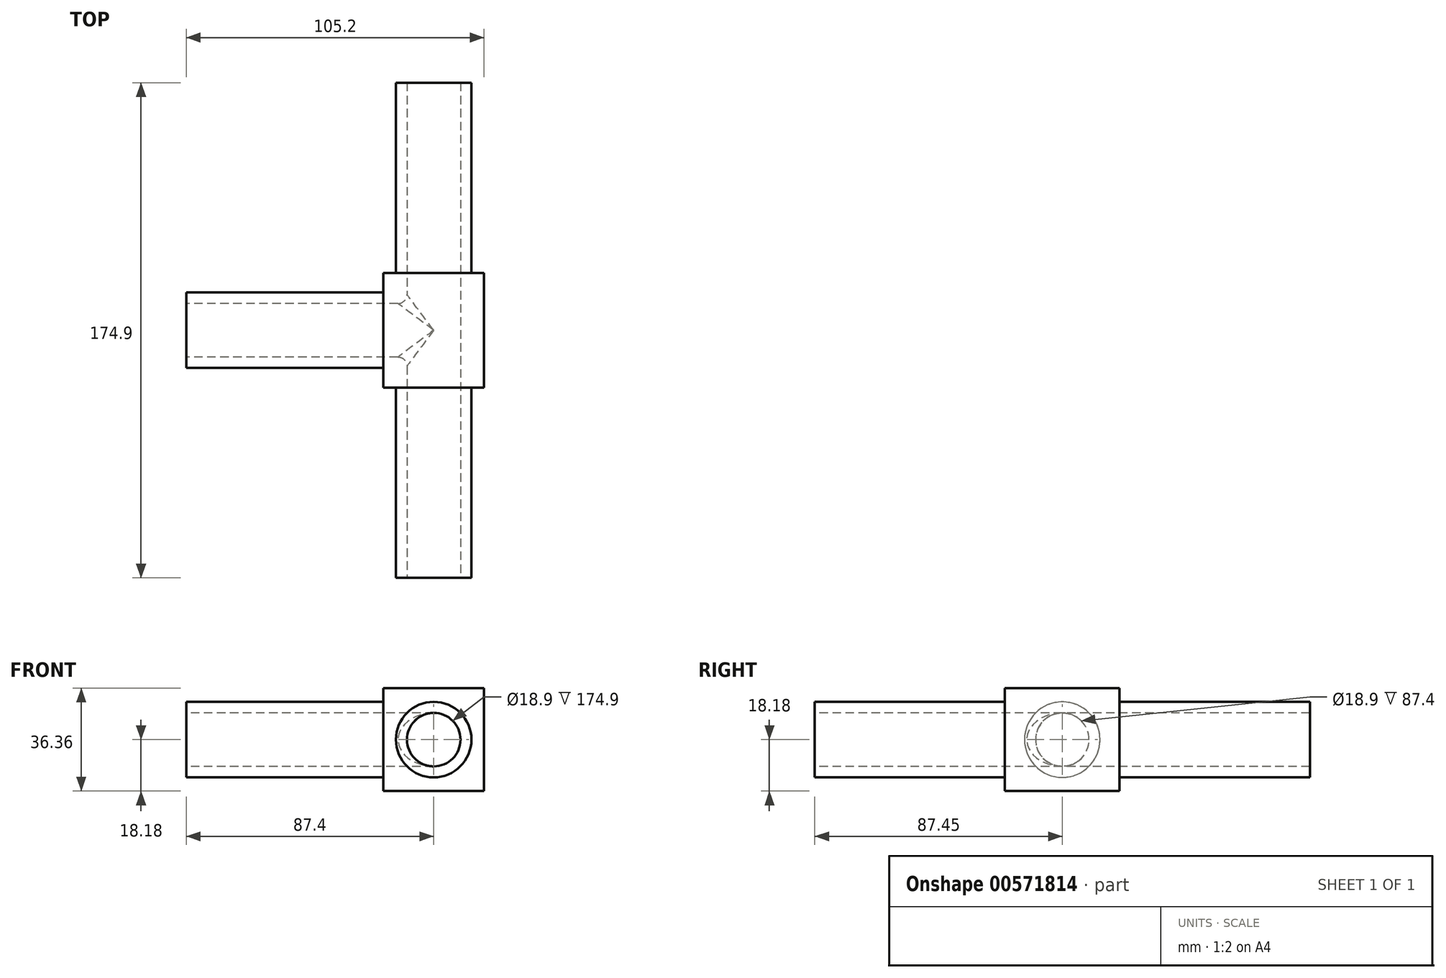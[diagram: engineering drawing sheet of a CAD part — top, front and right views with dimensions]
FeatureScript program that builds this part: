
annotation { "Feature Type Name" : "Feature", "Feature Type Description" : "" }
export const myFeature = defineFeature(function(context is Context, id is Id, definition is map)
    precondition{}
    {
        {
            var Q0;
            Q0=qCreatedBy(makeId("Front.planeOp"),FACE);
            var sketch = newSketch(context, id + "F0", { "sketchPlane" : qUnion([Q0])});
            skLineSegment(sketch, "E0.bottom", {"start": v(-17.8, -18.18) * mm, "end": v(17.8, -18.18) * mm});
            skLineSegment(sketch, "E0.top", {"start": v(-17.8, 18.18) * mm, "end": v(17.8, 18.18) * mm});
            skLineSegment(sketch, "E0.left", {"start": v(-17.8, -18.18) * mm, "end": v(-17.8, 18.18) * mm});
            skLineSegment(sketch, "E0.right", {"start": v(17.8, -18.18) * mm, "end": v(17.8, 18.18) * mm});
            skPoint(sketch, "E0.middle", {"position": v(0, 0) * mm});
            skSolve(sketch);
        }
        {
            var Q0;
            Q0 = qSketchRegion(id + "F0", true);
            extrude(context, id + "F1", {"entities" : qUnion([Q0]), "endBound" : BoundingType.SYMMETRIC, "depth" : 174.9 * mm, "offsetDistance" : 25 * mm});
        }
        {
            var Q0;
            Q0=makeQuery(id+"F1.opExtrude","CAP_FACE",FACE,{"disambiguationData":[OSD([sQuery(id+"F0.wireOp",EDGE,"E0.bottom"),sQuery(id+"F0.wireOp",EDGE,"E0.top"),sQuery(id+"F0.wireOp",EDGE,"E0.left"),sQuery(id+"F0.wireOp",EDGE,"E0.right")])],"isStart":false});
            var sketch = newSketch(context, id + "F2", { "sketchPlane" : qUnion([Q0])});
            skCircle(sketch, "E1", {"center": v(0, 0) * mm, "radius": 9.45 * mm});
            skSolve(sketch);
        }
        {
            var Q0;
            Q0 = qSketchRegion(id + "F2", true);
            extrude(context, id + "F3", {"entities" : qUnion([Q0]), "operationType" : NewBodyOperationType.REMOVE, "oppositeDirection" : true, "depth" : 206.4 * mm, "offsetDistance" : 25 * mm});
        }
        {
            var Q0;
            Q0=qCreatedBy(makeId("Right.planeOp"),FACE);
            var sketch = newSketch(context, id + "F4", { "sketchPlane" : qUnion([Q0])});
            skCircle(sketch, "E2", {"center": v(0, 0) * mm, "radius": 13.34 * mm});
            skSolve(sketch);
        }
        {
            var Q0;
            Q0 = qSketchRegion(id + "F4", true);
            extrude(context, id + "F5", {"entities" : qUnion([Q0]), "operationType" : NewBodyOperationType.ADD, "oppositeDirection" : true, "depth" : 87.4 * mm, "offsetDistance" : 25 * mm});
        }
        {
            var Q0;
            Q0=makeQuery(id+"F5.opExtrude","CAP_FACE",FACE,{"disambiguationData":[OSD([sQuery(id+"F4.wireOp",EDGE,"E2")])],"isStart":false});
            var sketch = newSketch(context, id + "F6", { "sketchPlane" : qUnion([Q0])});
            skCircle(sketch, "E3", {"center": v(0, 0) * mm, "radius": 9.45 * mm});
            skSolve(sketch);
        }
        {
            var Q0;
            Q0 = qSketchRegion(id + "F6", true);
            extrude(context, id + "F7", {"entities" : qUnion([Q0]), "operationType" : NewBodyOperationType.REMOVE, "oppositeDirection" : true, "depth" : 87.4 * mm, "offsetDistance" : 25 * mm});
        }
        {
            var Q0;
            Q0=makeQuery(id+"F1.opExtrude","CAP_FACE",FACE,{"disambiguationData":[OSD([sQuery(id+"F0.wireOp",EDGE,"E0.bottom"),sQuery(id+"F0.wireOp",EDGE,"E0.top"),sQuery(id+"F0.wireOp",EDGE,"E0.left"),sQuery(id+"F0.wireOp",EDGE,"E0.right")])],"isStart":false});
            var sketch = newSketch(context, id + "F8", { "sketchPlane" : qUnion([Q0])});
            skCircle(sketch, "E4", {"center": v(0, 0) * mm, "radius": 9.45 * mm});
            skSolve(sketch);
        }
        {
            var Q0;
            Q0 = qSketchRegion(id + "F8", true);
            extrude(context, id + "F9", {"entities" : qUnion([Q0]), "operationType" : NewBodyOperationType.REMOVE, "oppositeDirection" : true, "depth" : 231.3 * mm, "offsetDistance" : 25 * mm});
        }
        {
            var Q0;
            Q0=makeQuery(id+"F9.boolean.opBoolean","INTERSECT",EDGE,{"disambiguationData":[OD(1.0)],"derivedFrom":[makeQuery(id+"F7.boolean.opBoolean","COPY",FACE,{"derivedFrom":makeQuery(id+"F7.opExtrude","SWEPT_FACE",FACE,{"disambiguationData":[OSD([sQuery(id+"F6.wireOp",EDGE,"E3")])]})}),makeQuery(id+"F9.opExtrude","SWEPT_FACE",FACE,{"disambiguationData":[OSD([sQuery(id+"F8.wireOp",EDGE,"E4")])]})]});
            var Q1;
            Q1=makeQuery(id+"F9.boolean.opBoolean","INTERSECT",EDGE,{"disambiguationData":[OD(0.0)],"derivedFrom":[makeQuery(id+"F7.boolean.opBoolean","COPY",FACE,{"derivedFrom":makeQuery(id+"F7.opExtrude","SWEPT_FACE",FACE,{"disambiguationData":[OSD([sQuery(id+"F6.wireOp",EDGE,"E3")])]})}),makeQuery(id+"F9.opExtrude","SWEPT_FACE",FACE,{"disambiguationData":[OSD([sQuery(id+"F8.wireOp",EDGE,"E4")])]})]});
            fillet(context, id + "F10", {"entities" : qUnion([Q0, Q1]), "radius" : 3.2 * mm, "tangentPropagation" : true, "allowEdgeOverflow" : false});
        }
        {
            var Q0;
            Q0=makeQuery(id+"F1.opExtrude","CAP_FACE",FACE,{"disambiguationData":[OSD([sQuery(id+"F0.wireOp",EDGE,"E0.bottom"),sQuery(id+"F0.wireOp",EDGE,"E0.top"),sQuery(id+"F0.wireOp",EDGE,"E0.left"),sQuery(id+"F0.wireOp",EDGE,"E0.right")])],"isStart":false});
            var sketch = newSketch(context, id + "F11", { "sketchPlane" : qUnion([Q0])});
            skCircle(sketch, "E5", {"center": v(0, 0) * mm, "radius": 13.34 * mm});
            skCircle(sketch, "E6", {"center": v(0, 0) * mm, "radius": 30.92 * mm});
            skSolve(sketch);
        }
        {
            var Q0;
            Q0 = qSketchRegion(id + "F11", true);
            extrude(context, id + "F12", {"entities" : qUnion([Q0]), "operationType" : NewBodyOperationType.REMOVE, "oppositeDirection" : true, "depth" : 67.2 * mm, "offsetDistance" : 25 * mm});
        }
        {
            var Q0;
            Q0=makeQuery(id+"F1.opExtrude","CAP_FACE",FACE,{"disambiguationData":[OSD([sQuery(id+"F0.wireOp",EDGE,"E0.bottom"),sQuery(id+"F0.wireOp",EDGE,"E0.top"),sQuery(id+"F0.wireOp",EDGE,"E0.left"),sQuery(id+"F0.wireOp",EDGE,"E0.right")])],"isStart":true});
            var sketch = newSketch(context, id + "F13", { "sketchPlane" : qUnion([Q0])});
            skCircle(sketch, "E7", {"center": v(0, 0) * mm, "radius": 13.34 * mm});
            skCircle(sketch, "E8", {"center": v(0, 0) * mm, "radius": 36.42 * mm});
            skSolve(sketch);
        }
        {
            var Q0;
            Q0 = qSketchRegion(id + "F13", true);
            extrude(context, id + "F14", {"entities" : qUnion([Q0]), "operationType" : NewBodyOperationType.REMOVE, "oppositeDirection" : true, "depth" : 67.2 * mm, "offsetDistance" : 25 * mm});
        }
    });
